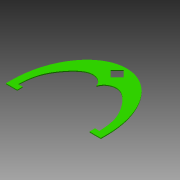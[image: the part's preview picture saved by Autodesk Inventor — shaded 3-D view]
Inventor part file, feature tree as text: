
AUTODESK INVENTOR PART (.ipt)
format: ipt  version: 2015 SP1 (Build 190203100, 203)  size: 124,416 bytes
history: native  units: mm
features: extrude x1
ambient origin geometry x8: Origin, YZ Plane, XZ Plane, XY Plane, X Axis, Y Axis, Z Axis, Center Point
bodies: Solid1 (feature_tree)
feature tree (1):
  extrude  "Extrusion1"  Depth=105.0mm
